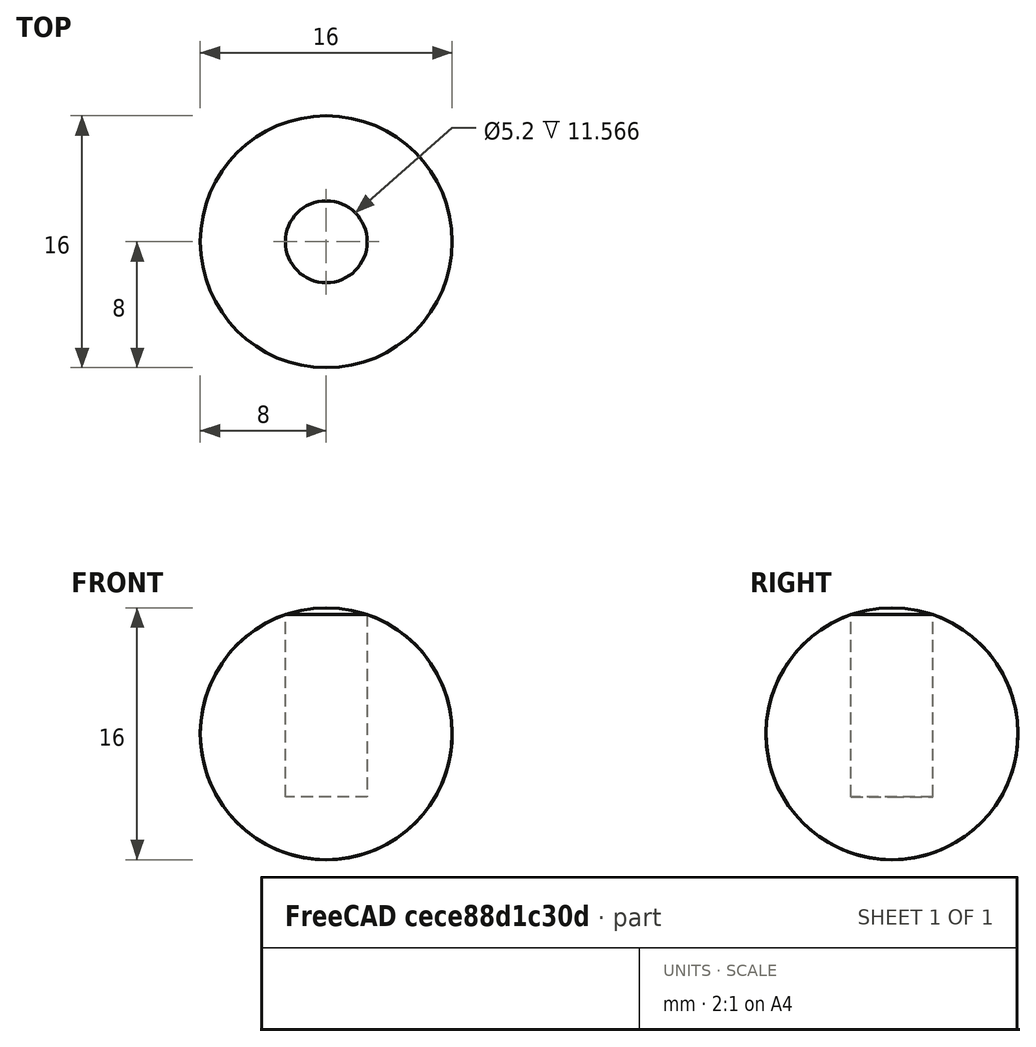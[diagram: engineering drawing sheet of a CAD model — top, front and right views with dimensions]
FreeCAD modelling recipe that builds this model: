
FCSTD DOCUMENT  (FreeCAD 0.18R4 (GitTag))
Label: landing_gear_foot
License: All rights reserved
LicenseURL: http://en.wikipedia.org/wiki/All_rights_reserved
objects: Part::Sphere×1, Sketcher::SketchObject×1, PartDesign::Pocket×1, PartDesign::Body×1, Mesh::Feature×1
note: 5 computed .brp shape members not serialized (recipe doc carries the construction recipe); baked Part::Feature solids carry a one-line shape summary decoded from their .brp

FEATURE [Part::Sphere] Sphere
  Angle1 = -90
  Angle2 = 90
  Angle3 = 360
  AttacherType = Attacher::AttachEngine3D
  Placement = pos=(0,0,-8) rot=(0,0,1;0rad)
  Radius = 8
FEATURE [Sketcher::SketchObject] Sketch
  Support = -> [Sphere]
  sketch-geometry (1):
    g0: Circle CenterX=0 CenterY=0 CenterZ=0 NormalX=0 NormalY=0 NormalZ=1 AngleXU=0 Radius=2.6
  constraints (2):
    c: Coincident(g0,g-1)
    c: Radius(g0) = 2.6
FEATURE [PartDesign::Pocket] Pocket
  Length = 12
  Length2 = 100
  Placement = pos=(0,0,-8) rot=(0,0,1;0rad)
  Profile = -> Sketch
  Type = 0
FEATURE [PartDesign::Body] Body  label="LandingGear"
  Group = -> [Sketch,Pocket]
  Origin = -> Origin
  Tip = -> Pocket
FEATURE [Mesh::Feature] Mesh  label="landing_gear_foot"
